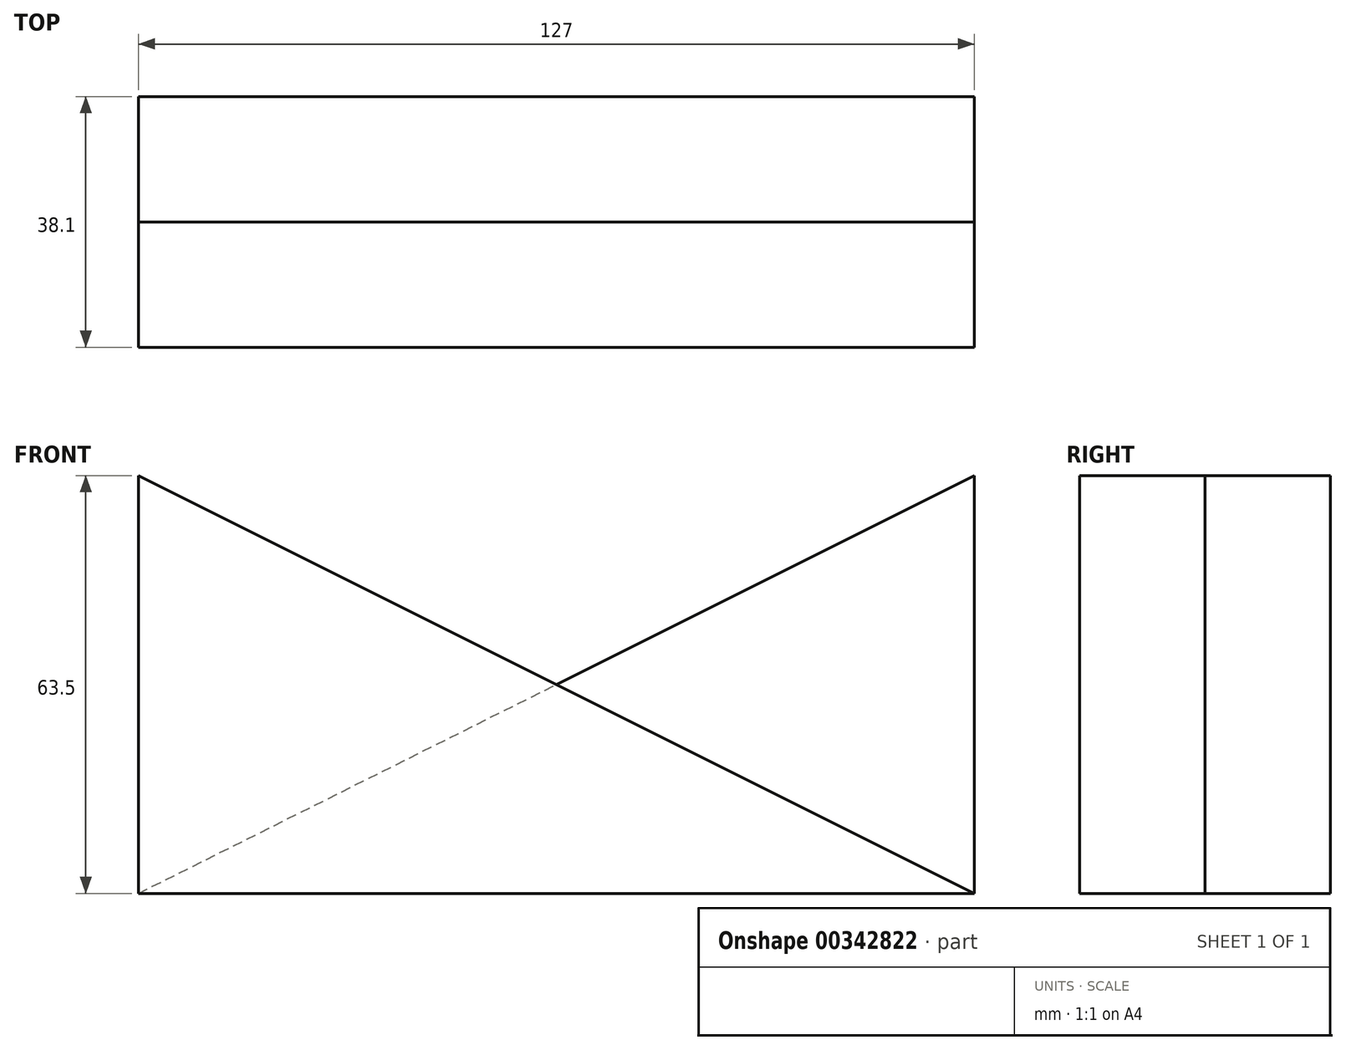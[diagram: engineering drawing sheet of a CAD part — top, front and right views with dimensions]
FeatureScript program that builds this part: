
annotation { "Feature Type Name" : "Feature", "Feature Type Description" : "" }
export const myFeature = defineFeature(function(context is Context, id is Id, definition is map)
    precondition{}
    {
        {
            var Q0;
            Q0=qCreatedBy(makeId("Front.planeOp"),FACE);
            var sketch = newSketch(context, id + "F0", { "sketchPlane" : qUnion([Q0])});
            skLineSegment(sketch, "E0", {"start": v(-55.47, 25.22) * mm, "end": v(-55.47, -38.28) * mm});
            skLineSegment(sketch, "E1", {"start": v(-55.47, -38.28) * mm, "end": v(71.53, -38.28) * mm});
            skLineSegment(sketch, "E2", {"start": v(-55.47, 25.22) * mm, "end": v(71.53, -38.28) * mm});
            skSolve(sketch);
        }
        {
            var Q0;
            Q0=makeQuery(id+"F0.imprint","IMPRINT",FACE,{"disambiguationData":[TD([[makeQuery(id+"F0.imprint","IMPRINT",EDGE,{"derivedFrom":sQuery(id+"F0.wireOp",EDGE,"E0")}),1.0]])]});
            extrude(context, id + "F1", {"entities" : qUnion([Q0]), "depth" : 19.05 * mm});
        }
        {
            var Q0;
            Q0=makeQuery(id+"F1.opExtrude","CAP_FACE",FACE,{"disambiguationData":[OSD([sQuery(id+"F0.wireOp",EDGE,"E0"),sQuery(id+"F0.wireOp",EDGE,"E1"),sQuery(id+"F0.wireOp",EDGE,"E2")])],"isStart":true});
            var sketch = newSketch(context, id + "F2", { "sketchPlane" : qUnion([Q0])});
            skLineSegment(sketch, "E3", {"start": v(-71.53, 25.22) * mm, "end": v(-71.53, -38.28) * mm});
            skLineSegment(sketch, "E4", {"start": v(-71.53, -38.28) * mm, "end": v(55.47, -38.28) * mm});
            skLineSegment(sketch, "E5", {"start": v(55.47, -38.28) * mm, "end": v(-71.53, 25.22) * mm});
            skSolve(sketch);
        }
        {
            var Q0;
            {var subQ0=sQuery(id+"F2.wireOp",EDGE,"E4");Q0=makeQuery(id+"F2.imprint","IMPRINT",FACE,{"disambiguationData":[TD([[makeQuery(id+"F2.imprint","IMPRINT",EDGE,{"derivedFrom":subQ0}),-1.0]])]});}
            var Q1;
            {var subQ0=sQuery(id+"F2.wireOp",EDGE,"E3");Q1=makeQuery(id+"F2.imprint","IMPRINT",FACE,{"disambiguationData":[TD([[makeQuery(id+"F2.imprint","IMPRINT",EDGE,{"derivedFrom":subQ0}),1.0]])]});}
            extrude(context, id + "F3", {"entities" : qUnion([Q0, Q1]), "operationType" : NewBodyOperationType.ADD, "depth" : 19.05 * mm});
        }
    });
